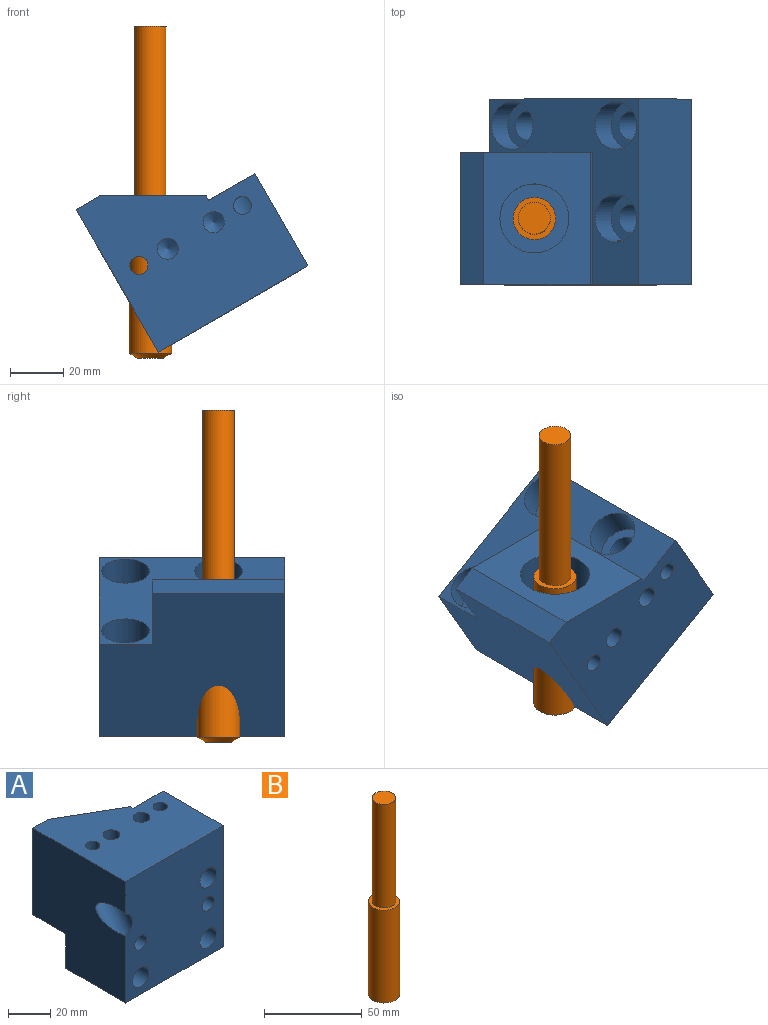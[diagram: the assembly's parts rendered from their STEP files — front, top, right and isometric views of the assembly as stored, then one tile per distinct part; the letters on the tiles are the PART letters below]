
ASSEMBLY  parts=2 mates=1
PART A: 33 faces, bbox 74.7x65x71.1 mm
  f0: cylinder r=7mm len=44.93mm, axis (0.5,0.87,0), area 1563.4mm2, adj f10,f21,f23,f31,f32
  f1: cylinder r=13mm len=30.02mm, axis (0.5,0.87,0), area 1225.2mm2, adj f19,f32
  f2: cylinder r=4mm len=16mm, axis (0,0,1), area 402.1mm2, adj f3,f26
  f3: cone r=4mm half-angle=59deg, axis (0,0,1), area 58.6mm2, adj f2
  f4: cylinder r=4mm len=16mm, axis (0,0,1), area 402.1mm2, adj f5,f26
  f5: cone r=4mm half-angle=59deg, axis (0,0,1), area 58.6mm2, adj f4
  f6: cylinder r=4mm len=24mm, axis (0,-1,0), area 603.2mm2, adj f7,f23
  f7: cone r=4mm half-angle=59deg, axis (0,-1,0), area 58.6mm2, adj f6
  f8: cylinder r=4mm len=24mm, axis (0,-1,0), area 603.2mm2, adj f9,f23
  f9: cone r=4mm half-angle=59deg, axis (0,-1,0), area 58.6mm2, adj f8
  f10: cylinder r=3.4mm len=22.25mm, axis (0,0,1), area 427.4mm2, adj f0,f26,f31
  f11: cylinder r=3.4mm len=16.67mm, axis (0,0,1), area 348.9mm2, adj f16,f26
  f12: cylinder r=9mm len=18mm, axis (0,1,0), area 678.6mm2, adj f25,f30
  f13: cylinder r=5.5mm len=28mm, axis (0,1,0), area 967.6mm2, adj f23,f30
  f14: cylinder r=9mm len=18mm, axis (0,1,0), area 678.6mm2, adj f25,f29
  f15: cylinder r=5.5mm len=28mm, axis (0,1,0), area 967.6mm2, adj f23,f29
  f16: cylinder r=9mm len=18mm, axis (0,1,0), area 641.6mm2, adj f11,f25,f28
  f17: cylinder r=5.5mm len=28mm, axis (0,1,0), area 967.6mm2, adj f23,f28
  f18: plane 50x1.92mm, normal (1,0,0), area 95.9mm2, adj f19,f25,f26,f27
  f19: plane 50x34.78mm, normal (0.5,0.87,0), area 1477.2mm2, adj f1,f18,f20,f26,f27
  f20: plane 50x10.22mm, normal (0,1,0), area 510.9mm2, adj f19,f21,f26,f27
  f21: plane 70x62mm, normal (-1,0,0), area 3664.3mm2, adj f0,f20,f22,f23,f25,f26,f27
  f22: plane 65x40mm, normal (0,0,-1), area 2600mm2, adj f21,f23,f24,f25
  f23: plane 71.06x66.06mm, normal (0,-1,0), area 4122.7mm2, adj f0,f6,f8,f13,f15,f17,f21,f22
  f24: plane 70x40mm, normal (1,0,0), area 2800mm2, adj f22,f23,f25,f26
  f25: plane 70x65mm, normal (0,1,0), area 1536.6mm2, adj f12,f14,f16,f18,f21,f22,f24,f26
  f26: plane 65x62mm, normal (0,0,1), area 3067.6mm2, adj f2,f4,f10,f11,f18,f19,f20,f21
  f27: plane 45x22mm, normal (0,0,-1), area 640.8mm2, adj f18,f19,f20,f21,f25
  f28: plane 18x18mm, normal (0,1,0), area 159.4mm2, adj f16,f17
  f29: plane 18x18mm, normal (0,1,0), area 159.4mm2, adj f14,f15
  f30: plane 18x18mm, normal (0,1,0), area 159.4mm2, adj f12,f13
  f31: cone r=3.4mm half-angle=59deg, axis (0,0,1), area 4.6mm2, adj f0,f10
  f32: plane 26x22.52mm, normal (0.5,0.87,0), area 377mm2, adj f0,f1
PART B: 6 faces, bbox 16x16x125 mm
  f0: cylinder r=6mm len=65mm, axis (0,0,-1), area 2450.4mm2, adj f1,f4
  f1: plane 16x16mm, normal (0,0,1), area 88mm2, adj f0,f2
  f2: cylinder r=8mm len=58.27mm, axis (0,0,-1), area 2928.9mm2, adj f1,f5
  f3: plane 10x10mm, normal (0,0,-1), area 78.5mm2, adj f5
  f4: plane 12x12mm, normal (0,0,1), area 113.1mm2, adj f0
  f5: cone r=5mm half-angle=60deg, axis (0,0,1), area 141.5mm2, adj f2,f3
PLACE A rot(axis=(0.94,-0.25,0.25),93.8deg) t=(106.02,164.95,29.59)mm
PLACE B t=(103,119.95,27.4)mm
MATE slider A.f0 <-> B.f0  axis (0,0,1) through (103,119.95,51.36)mm
